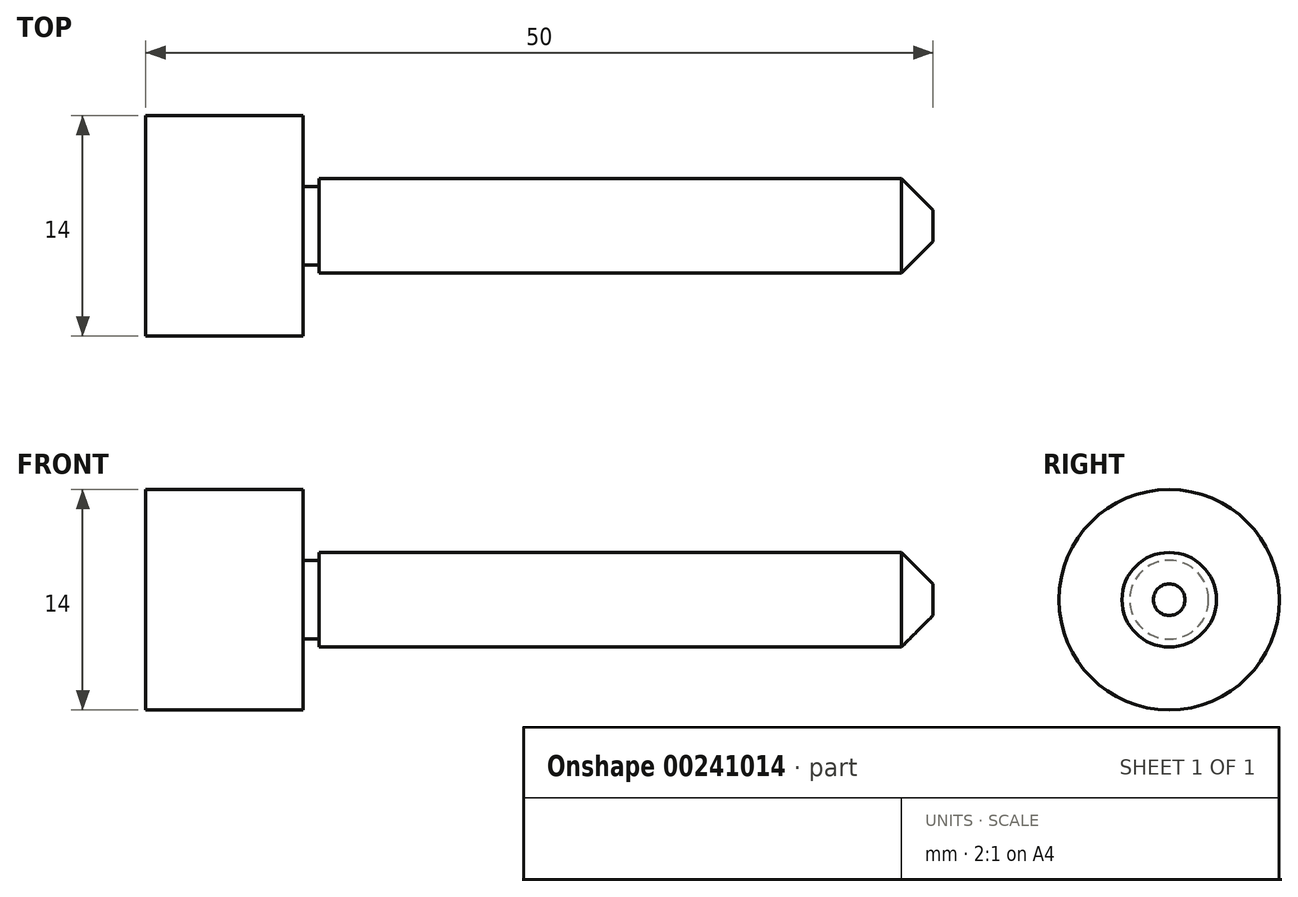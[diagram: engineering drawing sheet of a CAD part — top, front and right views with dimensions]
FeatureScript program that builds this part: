
annotation { "Feature Type Name" : "Feature", "Feature Type Description" : "" }
export const myFeature = defineFeature(function(context is Context, id is Id, definition is map)
    precondition{}
    {
        {
            var Q0;
            Q0=qCreatedBy(makeId("Front.planeOp"),FACE);
            var sketch = newSketch(context, id + "F0", { "sketchPlane" : qUnion([Q0])});
            skLineSegment(sketch, "E0", {"start": v(0, 0) * mm, "end": v(0, 7) * mm});
            skLineSegment(sketch, "E1", {"start": v(0, 7) * mm, "end": v(10, 7) * mm});
            skLineSegment(sketch, "E2", {"start": v(10, 7) * mm, "end": v(10, 2.5) * mm});
            skLineSegment(sketch, "E3", {"start": v(10, 2.5) * mm, "end": v(11, 2.5) * mm});
            skLineSegment(sketch, "E4", {"start": v(11, 2.5) * mm, "end": v(11, 3) * mm});
            skLineSegment(sketch, "E5", {"start": v(11, 3) * mm, "end": v(50, 3) * mm});
            skLineSegment(sketch, "E6", {"start": v(50, 3) * mm, "end": v(50, 0) * mm});
            skLineSegment(sketch, "E7", {"start": v(50, 0) * mm, "end": v(0, 0) * mm});
            skLineSegment(sketch, "E8", {"start": v(-4.08, 0) * mm, "end": v(52.6, 0) * mm, "construction": true});
            skSolve(sketch);
        }
        {
            var Q0;
            Q0=makeQuery(id+"F0.imprint","IMPRINT",FACE,{"disambiguationData":[TD([[makeQuery(id+"F0.imprint","IMPRINT",EDGE,{"derivedFrom":sQuery(id+"F0.wireOp",EDGE,"E0")}),-1.0]])]});
            var Q1;
            Q1=sQuery(id+"F0.wireOp",EDGE,"E8");
            revolve(context, id + "F1", {"entities" : qUnion([Q0]), "axis" : qUnion([Q1]), "revolveType" : RevolveType.FULL});
        }
        {
            var Q0;
            Q0=makeQuery(id+"F1.opRevolve","SWEPT_EDGE",EDGE,{"disambiguationData":[OSD([sQuery(id+"F0.wireOp",EDGE,"E5"),sQuery(id+"F0.wireOp",EDGE,"E6")])]});
            chamfer(context, id + "F2", {"entities" : qUnion([Q0]), "width" : 2 * mm, "tangentPropagation" : true});
        }
    });
